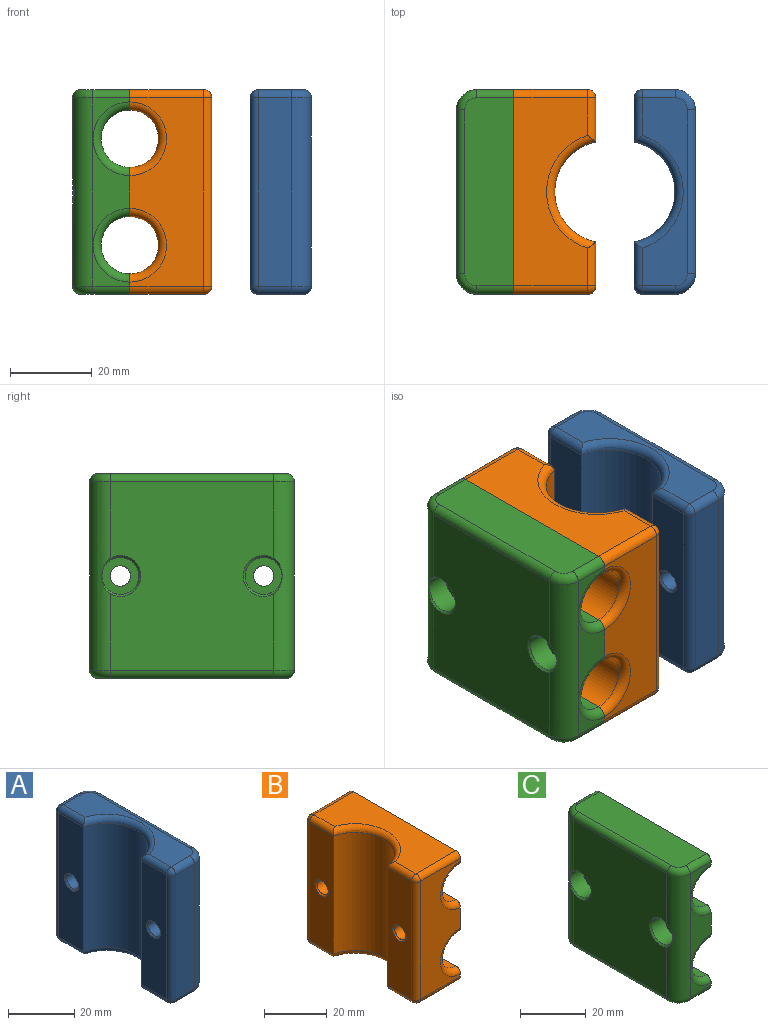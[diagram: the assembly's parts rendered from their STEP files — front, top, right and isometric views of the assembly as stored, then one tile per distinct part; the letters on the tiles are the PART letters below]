
ASSEMBLY  parts=3 mates=2
PART A: 38 faces, bbox 15.4x50.8x50 mm
  f0: plane 46x11mm, normal (0,0,1), area 300.3mm2, adj f10,f11,f13,f14,f16,f17,f32,f35
  f1: plane 46x11mm, normal (0,0,-1), area 300.3mm2, adj f18,f21,f22,f24,f25,f27,f34,f37
  f2: plane 46x10.75mm, normal (-1,0,0), area 466.3mm2, adj f9,f10,f15,f22,f28
  f3: plane 46x40mm, normal (1,0,0), area 1785.7mm2, adj f14,f21,f30,f31,f33,f36
  f4: plane 46x10.75mm, normal (-1,0,0), area 466.3mm2, adj f9,f16,f23,f27,f29
  f5: plane 46x8mm, normal (0,-1,0), area 368mm2, adj f17,f23,f24,f36
  f6: plane 46x8mm, normal (0,1,0), area 368mm2, adj f11,f15,f18,f33
  f7: cylinder r=2.5mm len=14mm, axis (-1,0,0), area 219.9mm2, adj f29,f31
  f8: cylinder r=2.5mm len=14mm, axis (-1,0,0), area 219.9mm2, adj f28,f30
  f9: cylinder r=12.5mm len=46mm, axis (0,0,1), area 1574.9mm2, adj f2,f4,f13,f25
  f10: cylinder r=2mm len=10.75mm, axis (0,1,0), area 32mm2, adj f0,f2,f12,f13
  f11: cylinder r=2mm len=8mm, axis (1,0,0), area 25.1mm2, adj f0,f6,f12,f32
  f12: sphere r=2mm, area 6.3mm2, adj f10,f11,f15
  f13: torus R=14.5mm, axis (0,0,-1), area 110mm2, adj f0,f9,f10,f16
  f14: cylinder r=2mm len=40mm, axis (0,-1,0), area 125.7mm2, adj f0,f3,f32,f35
  f15: cylinder r=2mm len=46mm, axis (0,0,1), area 144.5mm2, adj f2,f6,f12,f19
  f16: cylinder r=2mm len=10.75mm, axis (0,1,0), area 32mm2, adj f0,f4,f13,f20
  f17: cylinder r=2mm len=8mm, axis (-1,0,0), area 25.1mm2, adj f0,f5,f20,f35
  f18: cylinder r=2mm len=8mm, axis (-1,0,0), area 25.1mm2, adj f1,f6,f19,f34
  f19: sphere r=2mm, area 6.3mm2, adj f15,f18,f22
  f20: sphere r=2mm, area 6.3mm2, adj f16,f17,f23
  f21: cylinder r=2mm len=40mm, axis (0,1,0), area 125.7mm2, adj f1,f3,f34,f37
  f22: cylinder r=2mm len=10.75mm, axis (0,-1,0), area 32mm2, adj f1,f2,f19,f25
  f23: cylinder r=2mm len=46mm, axis (0,0,-1), area 144.5mm2, adj f4,f5,f20,f26
  f24: cylinder r=2mm len=8mm, axis (1,0,0), area 25.1mm2, adj f1,f5,f26,f37
  f25: torus R=14.5mm, axis (0,0,-1), area 110mm2, adj f1,f9,f22,f27
  f26: sphere r=2mm, area 6.3mm2, adj f23,f24,f27
  f27: cylinder r=2mm len=10.75mm, axis (0,-1,0), area 32mm2, adj f1,f4,f25,f26
  f28: cone r=2.5mm half-angle=45deg, axis (-1,0,0), area 12.2mm2, adj f2,f8
  f29: cone r=2.5mm half-angle=45deg, axis (-1,0,0), area 12.2mm2, adj f4,f7
  f30: cone r=2.5mm half-angle=45deg, axis (1,0,0), area 12.2mm2, adj f3,f8,f33
  f31: cone r=2.5mm half-angle=45deg, axis (1,0,0), area 12.2mm2, adj f3,f7,f36
  f32: torus R=3mm, axis (0,0,-1), area 21.1mm2, adj f0,f11,f14,f33
  f33: cylinder r=5mm len=46mm, axis (0,0,-1), area 360.2mm2, adj f3,f6,f30,f32,f34
  f34: torus R=3mm, axis (0,0,-1), area 21.1mm2, adj f1,f18,f21,f33
  f35: torus R=3mm, axis (0,0,-1), area 21.1mm2, adj f0,f14,f17,f36
  f36: cylinder r=5mm len=46mm, axis (0,0,1), area 360.2mm2, adj f3,f5,f31,f35,f37
  f37: torus R=3mm, axis (0,0,-1), area 21.1mm2, adj f1,f21,f24,f36
PART B: 38 faces, bbox 20x50x50 mm
  f0: plane 46x10.75mm, normal (-1,0,0), area 466.3mm2, adj f17,f19,f22,f28,f37
  f1: plane 50x12mm, normal (1,0,0), area 540mm2, adj f2,f8,f9,f10,f11,f12,f13,f14
  f2: cylinder r=7mm len=46mm, axis (0,-1,0), area 1011.6mm2, adj f1,f3,f11,f13
  f3: plane 50x5mm, normal (1,0,0), area 246.6mm2, adj f2,f4,f9,f10,f11,f13,f23,f29
  f4: plane 46x18mm, normal (0,0,1), area 626.1mm2, adj f3,f23,f28,f29,f31,f33
  f5: plane 46x10.75mm, normal (-1,0,0), area 466.3mm2, adj f17,f25,f30,f33,f36
  f6: plane 46x18mm, normal (0,0,-1), area 626.1mm2, adj f7,f18,f19,f21,f24,f25
  f7: plane 50x5mm, normal (1,0,0), area 246.6mm2, adj f6,f8,f9,f10,f12,f14,f18,f24
  f8: cylinder r=7mm len=46mm, axis (0,-1,0), area 1011.6mm2, adj f1,f7,f12,f14
  f9: plane 46x18mm, normal (0,-1,0), area 573.5mm2, adj f1,f3,f7,f13,f14,f24,f29,f30
  f10: plane 46x18mm, normal (0,1,0), area 573.5mm2, adj f1,f3,f7,f11,f12,f18,f22,f23
  f11: torus R=9mm, axis (0,-1,0), area 76.3mm2, adj f1,f2,f3,f10
  f12: torus R=9mm, axis (0,-1,0), area 76.3mm2, adj f1,f7,f8,f10
  f13: torus R=9mm, axis (0,-1,0), area 76.3mm2, adj f1,f2,f3,f9
  f14: torus R=9mm, axis (0,-1,0), area 76.3mm2, adj f1,f7,f8,f9
  f15: cylinder r=2.5mm len=19mm, axis (-1,0,0), area 298.5mm2, adj f35,f36
  f16: cylinder r=2.5mm len=19mm, axis (-1,0,0), area 298.5mm2, adj f34,f37
  f17: cylinder r=12.5mm len=46mm, axis (0,0,1), area 1574.9mm2, adj f0,f5,f21,f31
  f18: cylinder r=2mm len=18mm, axis (-1,0,0), area 56.5mm2, adj f6,f7,f10,f20
  f19: cylinder r=2mm len=10.75mm, axis (0,-1,0), area 32mm2, adj f0,f6,f20,f21
  f20: sphere r=2mm, area 6.3mm2, adj f18,f19,f22
  f21: torus R=14.5mm, axis (0,0,-1), area 110mm2, adj f6,f17,f19,f25
  f22: cylinder r=2mm len=46mm, axis (0,0,1), area 144.5mm2, adj f0,f10,f20,f26
  f23: cylinder r=2mm len=18mm, axis (1,0,0), area 56.5mm2, adj f3,f4,f10,f26
  f24: cylinder r=2mm len=18mm, axis (1,0,0), area 56.5mm2, adj f6,f7,f9,f27
  f25: cylinder r=2mm len=10.75mm, axis (0,-1,0), area 32mm2, adj f5,f6,f21,f27
  f26: sphere r=2mm, area 6.3mm2, adj f22,f23,f28
  f27: sphere r=2mm, area 6.3mm2, adj f24,f25,f30
  f28: cylinder r=2mm len=10.75mm, axis (0,1,0), area 32mm2, adj f0,f4,f26,f31
  f29: cylinder r=2mm len=18mm, axis (-1,0,0), area 56.5mm2, adj f3,f4,f9,f32
  f30: cylinder r=2mm len=46mm, axis (0,0,-1), area 144.5mm2, adj f5,f9,f27,f32
  f31: torus R=14.5mm, axis (0,0,-1), area 110mm2, adj f4,f17,f28,f33
  f32: sphere r=2mm, area 6.3mm2, adj f29,f30,f33
  f33: cylinder r=2mm len=10.75mm, axis (0,1,0), area 32mm2, adj f4,f5,f31,f32
  f34: cone r=2.5mm half-angle=45deg, axis (1,0,0), area 12.2mm2, adj f1,f16
  f35: cone r=2.5mm half-angle=45deg, axis (1,0,0), area 12.2mm2, adj f1,f15
  f36: cone r=2.5mm half-angle=45deg, axis (-1,0,0), area 12.2mm2, adj f5,f15
  f37: cone r=2.5mm half-angle=45deg, axis (-1,0,0), area 12.2mm2, adj f0,f16
PART C: 40 faces, bbox 14.4x50.8x50 mm
  f0: plane 10x9mm, normal (0,1,0), area 26.4mm2, adj f10,f17,f21,f35
  f1: plane 26x9mm, normal (0,1,0), area 106.8mm2, adj f6,f20,f21,f35
  f2: plane 10x9mm, normal (0,-1,0), area 26.4mm2, adj f8,f15,f22,f38
  f3: plane 26x9mm, normal (0,-1,0), area 106.8mm2, adj f6,f22,f23,f38
  f4: plane 46x12mm, normal (0,0,1), area 548.1mm2, adj f8,f14,f15,f16,f34,f37
  f5: plane 46x12mm, normal (0,0,-1), area 548.1mm2, adj f10,f17,f18,f19,f36,f39
  f6: plane 50x12mm, normal (1,0,0), area 540mm2, adj f1,f3,f7,f11,f20,f21,f22,f23
  f7: cylinder r=7mm len=46mm, axis (0,-1,0), area 1011.6mm2, adj f6,f8,f20,f22
  f8: plane 50x5mm, normal (1,0,0), area 246.6mm2, adj f2,f4,f7,f13,f14,f15,f20,f22
  f9: plane 46x40mm, normal (-1,0,0), area 1713.6mm2, adj f16,f19,f28,f29,f35,f38
  f10: plane 50x5mm, normal (1,0,0), area 246.6mm2, adj f0,f5,f11,f12,f17,f18,f21,f23
  f11: cylinder r=7mm len=46mm, axis (0,-1,0), area 1011.6mm2, adj f6,f10,f21,f23
  f12: plane 10x9mm, normal (0,-1,0), area 26.4mm2, adj f10,f18,f23,f38
  f13: plane 10x9mm, normal (0,1,0), area 26.4mm2, adj f8,f14,f20,f35
  f14: cylinder r=2mm len=9mm, axis (1,0,0), area 28.3mm2, adj f4,f8,f13,f34
  f15: cylinder r=2mm len=9mm, axis (-1,0,0), area 28.3mm2, adj f2,f4,f8,f37
  f16: cylinder r=2mm len=40mm, axis (0,1,0), area 125.7mm2, adj f4,f9,f34,f37
  f17: cylinder r=2mm len=9mm, axis (-1,0,0), area 28.3mm2, adj f0,f5,f10,f36
  f18: cylinder r=2mm len=9mm, axis (1,0,0), area 28.3mm2, adj f5,f10,f12,f39
  f19: cylinder r=2mm len=40mm, axis (0,-1,0), area 125.7mm2, adj f5,f9,f36,f39
  f20: torus R=9mm, axis (0,-1,0), area 76.3mm2, adj f1,f6,f7,f8,f13
  f21: torus R=9mm, axis (0,-1,0), area 76.3mm2, adj f0,f1,f6,f10,f11
  f22: torus R=9mm, axis (0,-1,0), area 76.3mm2, adj f2,f3,f6,f7,f8
  f23: torus R=9mm, axis (0,-1,0), area 76.3mm2, adj f3,f6,f10,f11,f12
  f24: cylinder r=4.5mm len=9mm, axis (-1,0,0), area 155.5mm2, adj f25,f28
  f25: plane 9x9mm, normal (-1,0,0), area 44mm2, adj f24,f31
  f26: cylinder r=4.5mm len=9mm, axis (-1,0,0), area 155.5mm2, adj f27,f29
  f27: plane 9x9mm, normal (-1,0,0), area 44mm2, adj f26,f30
  f28: cone r=4.5mm half-angle=45deg, axis (-1,0,0), area 17.6mm2, adj f9,f24,f38
  f29: cone r=4.5mm half-angle=45deg, axis (-1,0,0), area 17.6mm2, adj f9,f26,f35
  f30: cylinder r=2.5mm len=7.5mm, axis (-1,0,0), area 117.8mm2, adj f27,f32
  f31: cylinder r=2.5mm len=7.5mm, axis (-1,0,0), area 117.8mm2, adj f25,f33
  f32: cone r=2.5mm half-angle=45deg, axis (1,0,0), area 12.2mm2, adj f6,f30
  f33: cone r=2.5mm half-angle=45deg, axis (1,0,0), area 12.2mm2, adj f6,f31
  f34: torus R=3mm, axis (0,0,-1), area 21.1mm2, adj f4,f14,f16,f35
  f35: cylinder r=5mm len=46mm, axis (0,0,1), area 348.1mm2, adj f0,f1,f9,f13,f29,f34,f36
  f36: torus R=3mm, axis (0,0,-1), area 21.1mm2, adj f5,f17,f19,f35
  f37: torus R=3mm, axis (0,0,-1), area 21.1mm2, adj f4,f15,f16,f38
  f38: cylinder r=5mm len=46mm, axis (0,0,-1), area 348.1mm2, adj f2,f3,f9,f12,f28,f37,f39
  f39: torus R=3mm, axis (0,0,-1), area 21.1mm2, adj f5,f18,f19,f38
PLACE A t=(5.32,110.39,-25)mm
PLACE B rot(axis=(0,1,0),180deg) t=(-27.84,110.39,25)mm
PLACE C rot(axis=(0,1,0),0deg) t=(-38.05,110.39,-25)mm
MATE slider B.f0 <-> A.f2  axis (1,0,0) through (-15.95,103.02,0)mm
MATE fastened B.f15 <-> C.f24  axis (-1,0,0) through (-35.95,67.89,0)mm
